# Revit family: 3036880 Feilo Sylvania Lighting Fixture LUMISTRIP IP20 5M WW
name_source: partatom
category: Lighting Fixtures
revit_build: Autodesk Revit 2017 (Build: 20190507_1515(x64)
units: mm (PartAtom-declared; Revit-internal decimal feet)

## family parameters
Cut with Voids When Loaded = No
Host = Face
Light Source = Yes
OmniClass Number = 23.80.70.00
OmniClass Title = Lighting
Part Type = Normal
Room Calculation Point = No
Round Connector Dimension = Use Diameter
Shared = No

## types (5) — shared parameters
Apparent Load = 24 VA
Assembly Code = D5020200
AssetType = Fixed
ClassificationName = Uniclass2015
ClassificationValue = EF_70_80
Color Filter = 16777215
Default Elevation = 1219 mm
Description = 5 metre warm white IP20 LED reel with pre-attached 3M adhesive tape, 1780 lumens, 24W, 74lm/W, 24V, 3000K, IP20, 50,000hrs (L70), (LxWxD) 5000x8x3mm
Dimming Lamp Color Temperature Shift = <None>
DocumentationLiterature = http://www.sylvania-lighting.com
DurationUnit = hours
ElectricShockClassification = Class III
Emit Shape Visible in Rendering = No
Emit from Rectangle Width = 8 mm  [stored 0.0262467 ft]
ExpectedLife = 50000
Height_FEILO = 3 mm  [stored 0.00984252 ft]
IfcExportAs = IfcLightFixtureType
IfcExportType = IfcLightFixtureType
IngressProtection = IP20
InputVoltage = 24V DC
Keynote = 16500
Lamp = LED
LampColourRenderingIndex = 0
LampColourTemperature = 3000 K
LampNominalLuminous = 1780 (356/metre) lm
LampsType = LED
LightOutputRatio = 100
LuminousEfficacy = 70.62 lm/W
Manufacturer = Feilo Sylvania
ManufacturerName = Feilo Sylvania
Material_1_FEILO = LED-Sylvania-Lumistrip
Material_2_FEILO = Body-Sylvania-Lumistrip-Aluminium
Material_3_FEILO = Diffuser-Sylvania-Lumistrip-Transparent
Material_4_FEILO = <By Category>
Model = LUMISTRIP IP20 5M WW
ModelNumber = 3036880
ModelReference = LUMISTRIP IP20 5M WW
Name = LUMISTRIP IP20 5M WW
NominalDepth = 8 mm  [stored 0.0262467 ft]
NominalHeight = 3 mm  [stored 0.00984252 ft]
NominalLength = 5000 mm
Photometric Web File = 3036880.ies
PowerConsumption = 24 W
Radius_FEILO = 1 mm  [stored 0.00328084 ft]
Tilt Angle = -90.00°
Type Image = <None>
TypeName = LUMISTRIP IP20 5M WW
URL = http://www.sylvania-lighting.com
Voltage = 24 V
Weight = 3.2 kg
Width_FEILO = 8 mm  [stored 0.0262467 ft]
zero-valued in all types: Cost, PowerFactor

## per-type parameters (varying)
| type | Emit from Rectangle Length | Length_FEILO |
| 3036880 LUMISTRIP IP20 1M WW | 1000 mm  [stored 3.28084 ft] | 1000 mm  [stored 3.28084 ft] |
| 3036880 LUMISTRIP IP20 500MM WW | 500 mm  [stored 1.64042 ft] | 500 mm  [stored 1.64042 ft] |
| 3036880 LUMISTRIP IP20 100MM WW | 100 mm  [stored 0.328084 ft] | 100 mm  [stored 0.328084 ft] |
| 3036880 LUMISTRIP IP20 50MM WW | 50 mm | 50 mm |
| 3036880 LUMISTRIP IP20 20MM WW | 20 mm | 20 mm |

note: [stored X ft] marks values corroborated as IEEE doubles in the binary element streams (Revit-internal decimal feet)

## geometry (parser evidence)
native form markers: Sweep x1
no freeform markers — native parametric forms only
